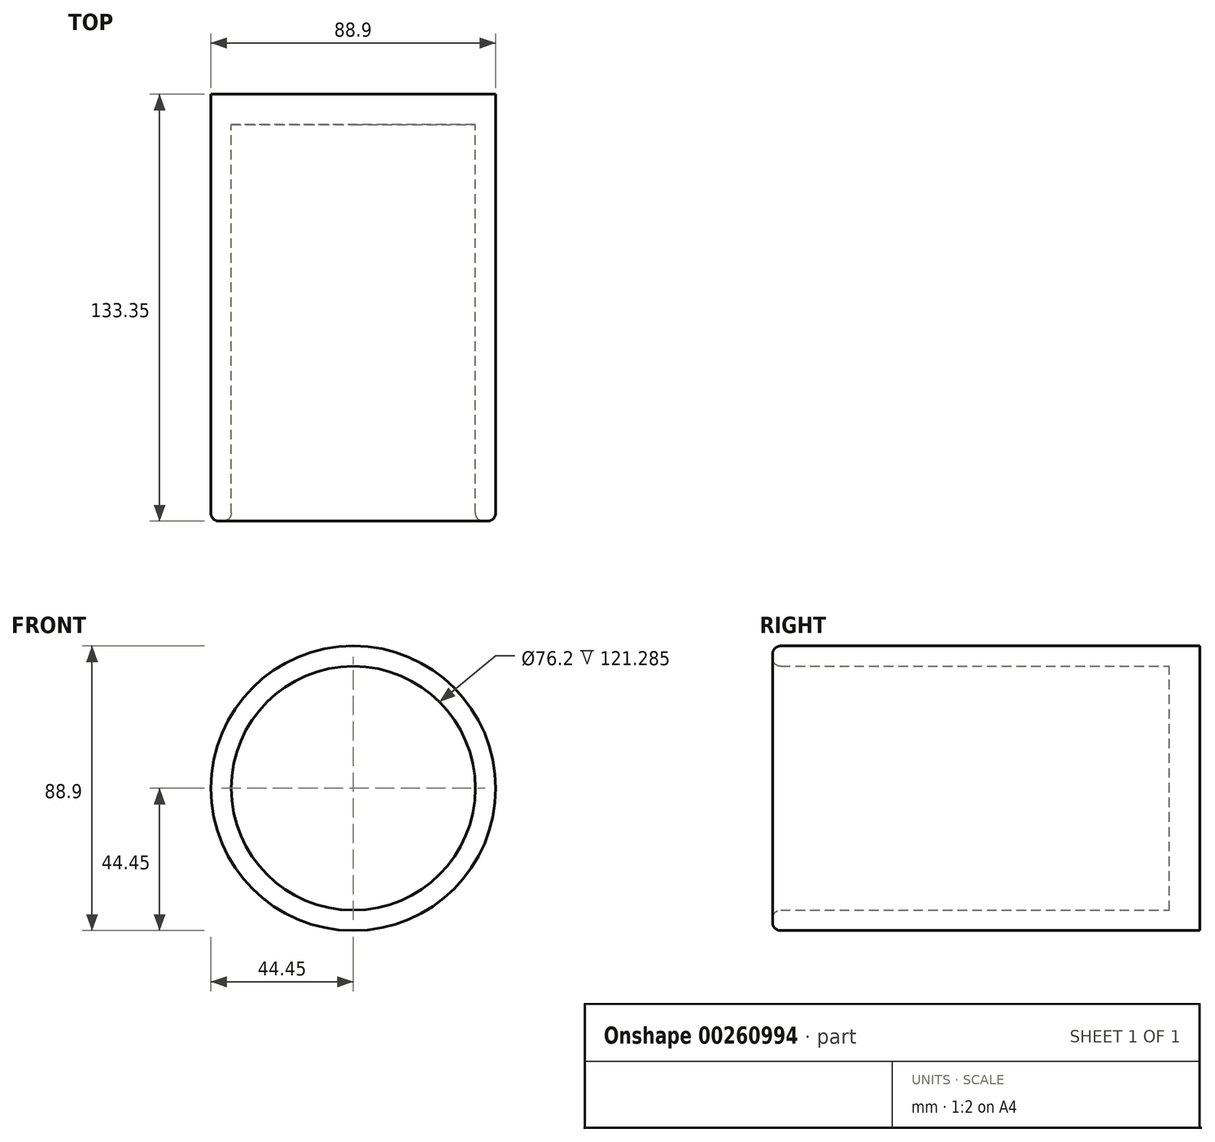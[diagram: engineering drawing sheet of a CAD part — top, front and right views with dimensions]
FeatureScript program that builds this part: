
annotation { "Feature Type Name" : "Feature", "Feature Type Description" : "" }
export const myFeature = defineFeature(function(context is Context, id is Id, definition is map)
    precondition{}
    {
        {
            var Q0;
            Q0=qCreatedBy(makeId("Front.planeOp"),FACE);
            var sketch = newSketch(context, id + "F0", { "sketchPlane" : qUnion([Q0])});
            skCircle(sketch, "E0", {"center": v(0, 0) * mm, "radius": 38.1 * mm});
            skLineSegment(sketch, "E1", {"start": v(-38.1, 0) * mm, "end": v(-44.45, 0) * mm});
            skCircle(sketch, "E2", {"center": v(0, 0) * mm, "radius": 44.45 * mm});
            skSolve(sketch);
        }
        {
            var Q0;
            Q0=makeQuery(id+"F0.imprint","IMPRINT",FACE,{"disambiguationData":[TD([[makeQuery(id+"F0.imprint","IMPRINT",EDGE,{"derivedFrom":sQuery(id+"F0.wireOp",EDGE,"E0")}),-1.0]])]});
            extrude(context, id + "F1", {"entities" : qUnion([Q0]), "depth" : 123.82 * mm});
        }
        {
            var Q0;
            Q0 = qSketchRegion(id + "F0", true);
            extrude(context, id + "F2", {"entities" : qUnion([Q0]), "operationType" : NewBodyOperationType.ADD, "depth" : 25.4 * mm});
        }
        {
            var Q0;
            Q0=makeQuery(id+"F0.imprint","IMPRINT",FACE,{"disambiguationData":[TD([[makeQuery(id+"F0.imprint","IMPRINT",EDGE,{"derivedFrom":sQuery(id+"F0.wireOp",EDGE,"E0")}),1.0]])]});
            var Q1;
            Q1=makeQuery(id+"F1.opExtrude","CAP_FACE",FACE,{"disambiguationData":[OSD([sQuery(id+"F0.wireOp",EDGE,"E0"),sQuery(id+"F0.wireOp",EDGE,"E2")])],"isStart":false});
            extrude(context, id + "F3", {"entities" : qUnion([Q0, Q1]), "operationType" : NewBodyOperationType.ADD, "depth" : 9.52 * mm});
        }
        {
            var Q0;
            Q0=makeQuery(id+"F3.opExtrude","CAP_FACE",FACE,{"disambiguationData":[OSD([sQuery(id+"F0.wireOp",EDGE,"E0"),sQuery(id+"F0.wireOp",EDGE,"E2")])],"isStart":false});
            fillet(context, id + "F4", {"entities" : qUnion([Q0]), "radius" : 2.54 * mm, "tangentPropagation" : true, "allowEdgeOverflow" : false});
        }
    });
